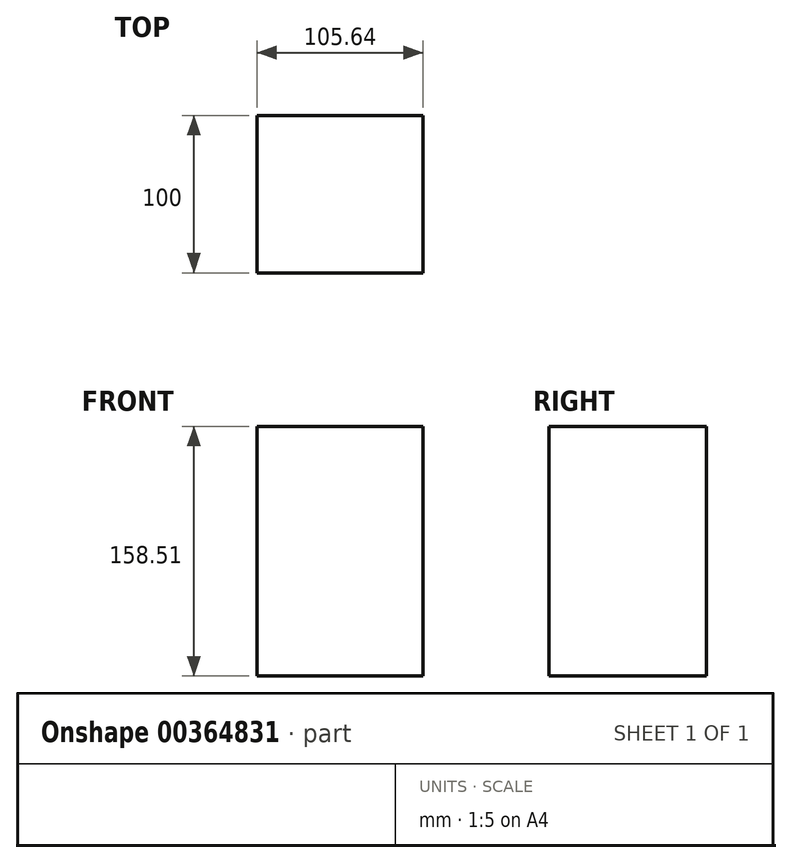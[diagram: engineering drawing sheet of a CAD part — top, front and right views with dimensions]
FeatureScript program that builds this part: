
annotation { "Feature Type Name" : "Feature", "Feature Type Description" : "" }
export const myFeature = defineFeature(function(context is Context, id is Id, definition is map)
    precondition{}
    {
        {
            var Q0;
            Q0=qCreatedBy(makeId("Front.planeOp"),FACE);
            var sketch = newSketch(context, id + "F0", { "sketchPlane" : qUnion([Q0])});
            skLineSegment(sketch, "E0.bottom", {"start": v(-55.52, 111.42) * mm, "end": v(50.12, 111.42) * mm});
            skLineSegment(sketch, "E0.top", {"start": v(-55.52, -47.1) * mm, "end": v(50.12, -47.1) * mm});
            skLineSegment(sketch, "E0.left", {"start": v(-55.52, 111.42) * mm, "end": v(-55.52, -47.1) * mm});
            skLineSegment(sketch, "E0.right", {"start": v(50.12, 111.42) * mm, "end": v(50.12, -47.1) * mm});
            skSolve(sketch);
        }
        {
            var Q0;
            Q0=makeQuery(id+"F0.imprint","IMPRINT",FACE,{"disambiguationData":[TD([[makeQuery(id+"F0.imprint","IMPRINT",EDGE,{"derivedFrom":sQuery(id+"F0.wireOp",EDGE,"E0.bottom")}),-1.0]])]});
            extrude(context, id + "F1", {"entities" : qUnion([Q0]), "endBound" : BoundingType.SYMMETRIC, "depth" : 100 * mm});
        }
    });
